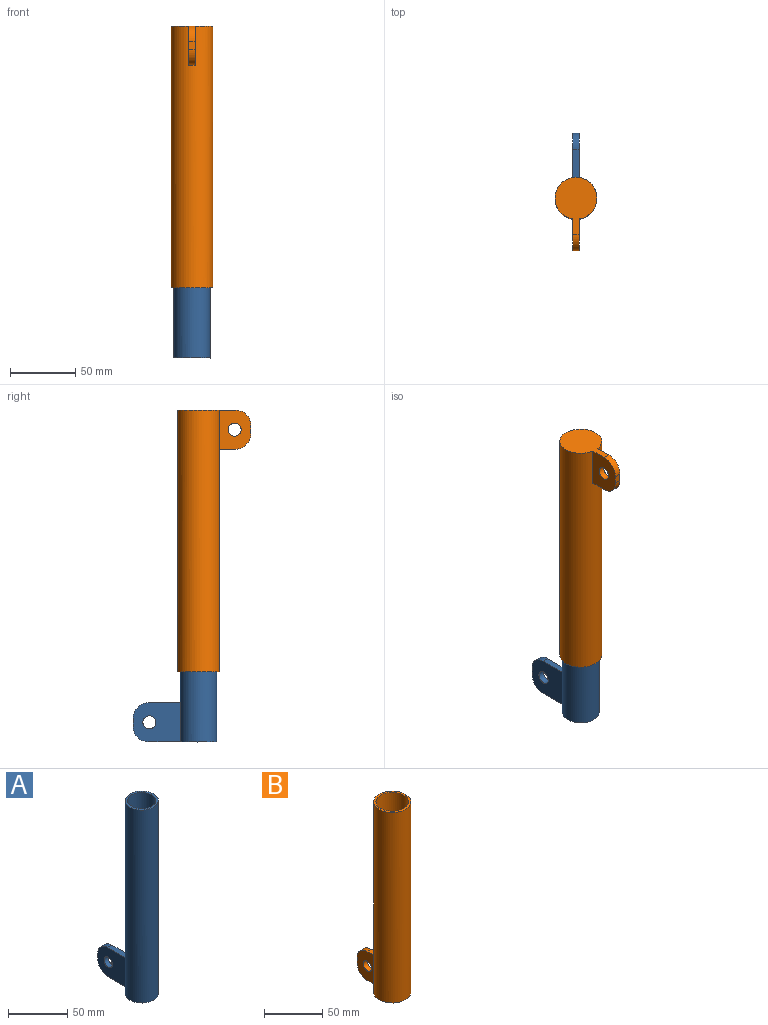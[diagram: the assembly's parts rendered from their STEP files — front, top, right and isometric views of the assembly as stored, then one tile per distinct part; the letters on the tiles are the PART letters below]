
ASSEMBLY  parts=2 mates=1
PART A: 12 faces, bbox 28x64x200 mm
  f0: cylinder r=12mm len=198mm, axis (0,0,-1), area 14928.8mm2, adj f2,f11
  f1: cylinder r=14mm len=200mm, axis (0,0,-1), area 17442.1mm2, adj f2,f3,f5,f6,f7
  f2: plane 28x28mm, normal (0,0,1), area 163.4mm2, adj f0,f1
  f3: plane 52x28mm, normal (0,0,-1), area 736.1mm2, adj f1,f6,f7,f9
  f4: plane 6x5mm, normal (0,1,0), area 30mm2, adj f6,f7,f9,f10
  f5: plane 24.25x5mm, normal (0,0,1), area 120.4mm2, adj f1,f6,f7,f10
  f6: plane 36.2x30mm, normal (1,0,0), area 945.7mm2, adj f1,f3,f4,f5,f8,f9,f10
  f7: plane 36.25x30mm, normal (-1,0,0), area 947.1mm2, adj f1,f3,f4,f5,f8,f9,f10
  f8: cylinder r=5mm len=10mm, axis (-1,0,0), area 157.1mm2, adj f6,f7
  f9: cylinder r=12mm len=12mm, axis (1,0,0), area 94.2mm2, adj f3,f4,f6,f7
  f10: cylinder r=12mm len=12mm, axis (1,0,0), area 94.2mm2, adj f4,f5,f6,f7
  f11: plane 24x24mm, normal (0,0,1), area 452.4mm2, adj f0
PART B: 12 faces, bbox 32x56x200 mm
  f0: cylinder r=14mm len=198mm, axis (0,0,-1), area 17417mm2, adj f2,f11
  f1: cylinder r=16mm len=200mm, axis (0,0,-1), area 19955.6mm2, adj f2,f3,f5,f6,f7
  f2: plane 32x32mm, normal (0,0,1), area 188.5mm2, adj f0,f1
  f3: plane 44x32mm, normal (0,0,-1), area 864.6mm2, adj f1,f6,f7,f9
  f4: plane 6x5mm, normal (0,1,0), area 30mm2, adj f6,f7,f9,f10
  f5: plane 12.22x5mm, normal (0,0,1), area 60.3mm2, adj f1,f6,f7,f10
  f6: plane 30x24.18mm, normal (1,0,0), area 584.9mm2, adj f1,f3,f4,f5,f8,f9,f10
  f7: plane 30x24.22mm, normal (-1,0,0), area 586.2mm2, adj f1,f3,f4,f5,f8,f9,f10
  f8: cylinder r=5mm len=10mm, axis (-1,0,0), area 157.1mm2, adj f6,f7
  f9: cylinder r=12mm len=12mm, axis (1,0,0), area 94.2mm2, adj f3,f4,f6,f7
  f10: cylinder r=12mm len=12mm, axis (1,0,0), area 94.2mm2, adj f4,f5,f6,f7
  f11: plane 28x28mm, normal (0,0,1), area 615.8mm2, adj f0
PLACE A t=(-53.65,16.16,116.23)mm
PLACE B rot(axis=(1,0,0),180deg) t=(-53.65,16.16,369.74)mm
MATE slider B.f0 <-> A.f1  axis (0,0,-1) through (-53.65,16.16,169.74)mm
